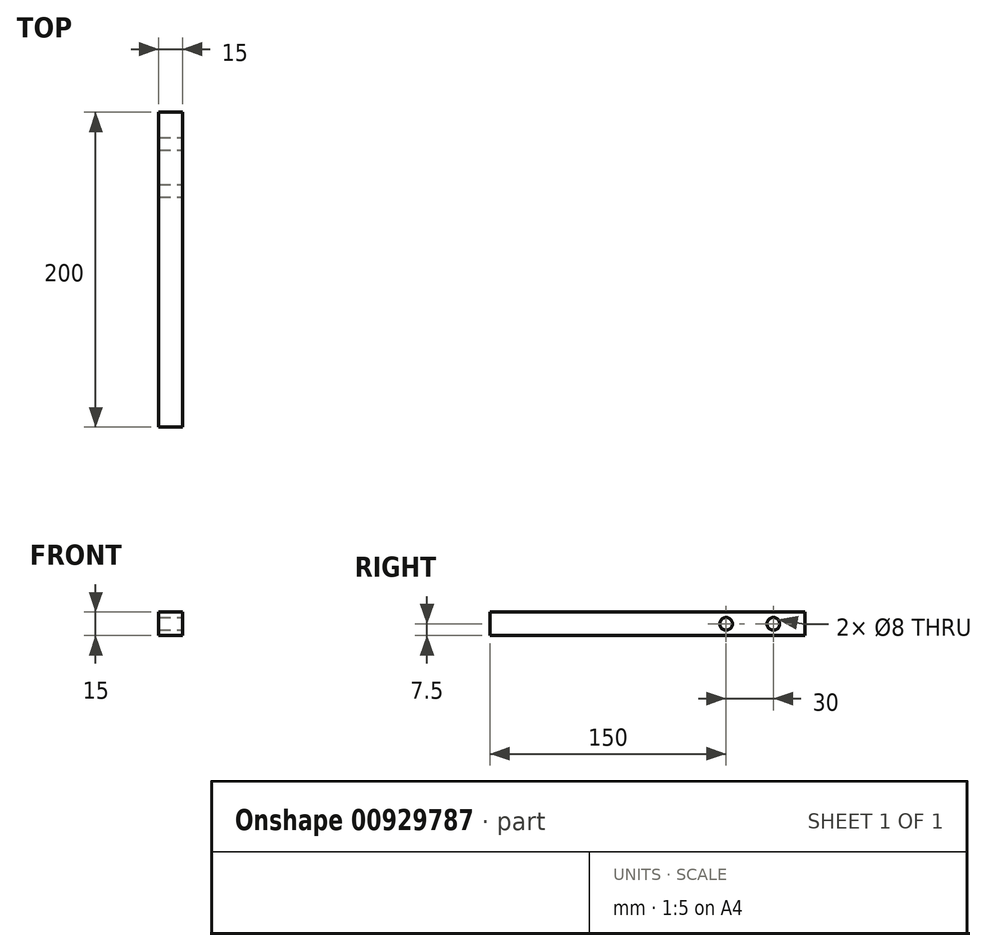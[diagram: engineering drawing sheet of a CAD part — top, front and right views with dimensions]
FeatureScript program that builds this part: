
annotation { "Feature Type Name" : "Feature", "Feature Type Description" : "" }
export const myFeature = defineFeature(function(context is Context, id is Id, definition is map)
    precondition{}
    {
        {
            var Q0;
            Q0=qCreatedBy(makeId("Top.planeOp"),FACE);
            var sketch = newSketch(context, id + "F0", { "sketchPlane" : qUnion([Q0])});
            skLineSegment(sketch, "E0.bottom", {"start": v(-7.5, -100) * mm, "end": v(7.5, -100) * mm});
            skLineSegment(sketch, "E0.top", {"start": v(-7.5, 100) * mm, "end": v(7.5, 100) * mm});
            skLineSegment(sketch, "E0.left", {"start": v(-7.5, -100) * mm, "end": v(-7.5, 100) * mm});
            skLineSegment(sketch, "E0.right", {"start": v(7.5, -100) * mm, "end": v(7.5, 100) * mm});
            skPoint(sketch, "E0.middle", {"position": v(0, 0) * mm});
            skSolve(sketch);
        }
        {
            var Q0;
            Q0 = qSketchRegion(id + "F0", true);
            extrude(context, id + "F1", {"entities" : qUnion([Q0]), "depth" : 15 * mm, "offsetDistance" : 25 * mm});
        }
        {
            var Q0;
            Q0=makeQuery(id+"F1.opExtrude","SWEPT_FACE",FACE,{"disambiguationData":[OSD([sQuery(id+"F0.wireOp",EDGE,"E0.right")])]});
            var sketch = newSketch(context, id + "F2", { "sketchPlane" : qUnion([Q0])});
            skLineSegment(sketch, "E1", {"start": v(100, 7.5) * mm, "end": v(-100, 7.5) * mm, "construction": true});
            skLineSegment(sketch, "E2", {"start": v(80, 0) * mm, "end": v(80, 15) * mm, "construction": true});
            skLineSegment(sketch, "E3", {"start": v(50, 0) * mm, "end": v(50, 15) * mm, "construction": true});
            skCircle(sketch, "E4", {"center": v(50, 7.5) * mm, "radius": 4 * mm});
            skCircle(sketch, "E5", {"center": v(80, 7.5) * mm, "radius": 4 * mm});
            skSolve(sketch);
        }
        {
            var Q0;
            Q0 = qSketchRegion(id + "F2", true);
            extrude(context, id + "F3", {"entities" : qUnion([Q0]), "operationType" : NewBodyOperationType.REMOVE, "endBound" : BoundingType.UP_TO_NEXT, "oppositeDirection" : true, "depth" : 25 * mm, "offsetDistance" : 25 * mm});
        }
    });
